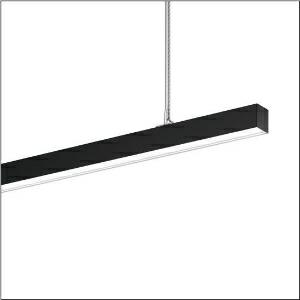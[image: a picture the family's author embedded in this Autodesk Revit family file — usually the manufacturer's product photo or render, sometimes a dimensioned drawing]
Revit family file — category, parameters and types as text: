
# Revit family: silica_r__21_51mx33dc4dbb_4870
name_source: partatom
category: Lighting Fixtures
units: mm (PartAtom-declared; Revit-internal decimal feet)

## family parameters
Cut with Voids When Loaded = No
Host = Face
Light Source = No
Part Type = Normal
Room Calculation Point = No
Round Connector Dimension = Use Diameter
Shared = No

## types (1)
- --- (1 x LED, 14790 lm, 93.9 W, 4000K)
    Apparent Load = 94 VA
    CIE Flux Codes = 78 96 99 55 100
    Color Rendering = 80
    Color Temperature = 4000K
    Default Elevation = 1800 mm
    Description = Silica® 21, office luminaire, primary optical cover: prismatic diffuser, of PMMA, CAT 2 (L<= 3000cd/m²), light emission: direct/indirect distribution, primary light characteristic: symmetric, installation type: suspended mounting, LED, rated luminous flux: 14.790lm, luminous efficacy: 158lm/W, light colour: 840, colour temperature: 4000K, control gear: DALI 2, with terminal, 3+2-pole, max. 2.5mm², mains connection: 220..240V, AC, 50/60Hz, rated input power: 93.9W, luminaire housing, of aluminium, matt jet black (RAL 9005), length: 3.004mm, width: 53mm, height: 53mm, protection rating (complete): IP20, insulation class (complete): insulation class I (protective earthing), certification: CE, permissible operating ambient temperature: 0..+35°C, standard: EN 50419, packaging unit: 1 piece
    Height = 53 mm
    Lamp = 1 x LED
    Lamp Light Flux = 14790 lm
    Lamp Power = 93.9 W
    Lamp count = 1
    Length = 3004 mm
    Luminous efficacy = 158 lm/W
    Manufacturer = Siteco
    ModVariant = No
    Model = 51MX33DC4DBB
    Mounting Place = Ceiling
    Mounting Type = Pendant
    Number of Poles = 1
    OnlyDefault = Yes
    Power Factor = 1
    Product Name = Silica® 21
    Product group = office luminaire | ceiling pendant
    ProductGroupID = 904
    Protection Class = Protection class I
    Protection Degree = IP 20
    RLX_Detail_Level = 1
    RLX_Emergency_Light_Flux = 0 lm
    RLX_Emergency_Type = 0
    RLX_Emergency_Type_DB = No
    RlxData = <blob elided: 26125 chars, md5=81657acd>
    Socket = socket
    Standby Power = 0 W
    System Light Flux = 14790 lm
    System Power = 94 W
    Type Comments = factory setting: luminous flux: 100 % | dim-lin: 254 | 323 mA
    Type Image = l_1335856.jpg
    URL = http://relux.com
    VarID = @adj_118670
    Voltage = 0 V
    Weight = 0.00 kg
    Width = 53 mm

## geometry (parser evidence)
native form markers: Blend x4, Sweep x12
no freeform markers — native parametric forms only
